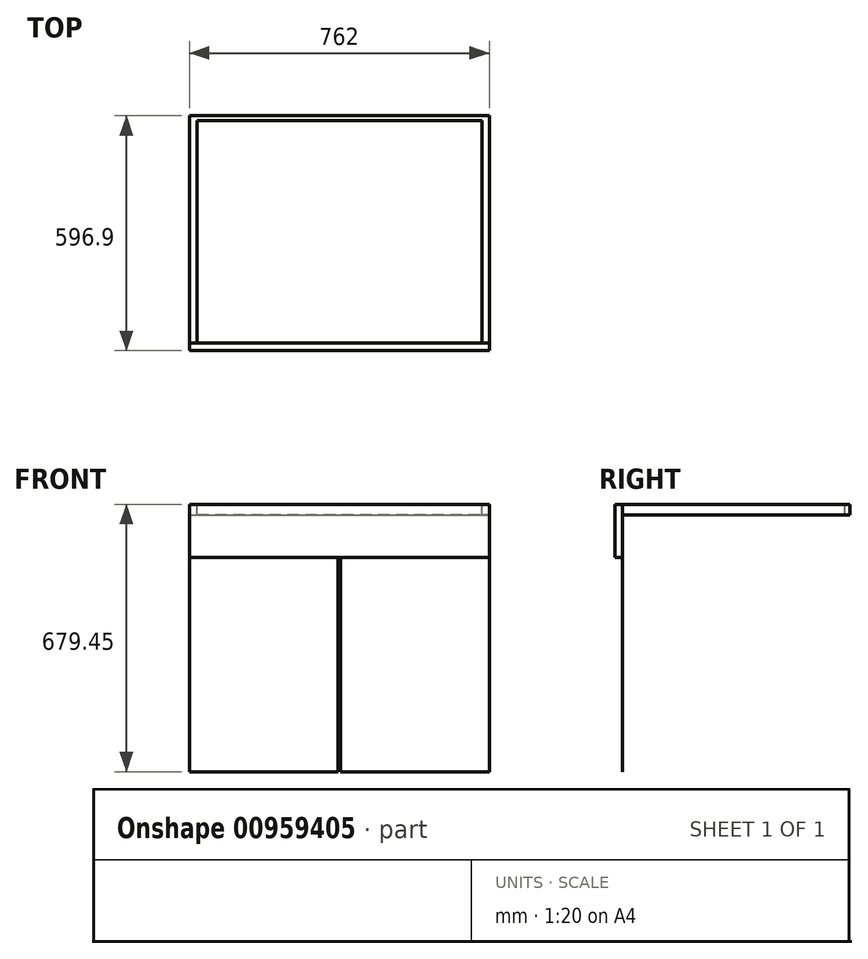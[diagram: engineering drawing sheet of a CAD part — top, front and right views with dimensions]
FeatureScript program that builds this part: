
annotation { "Feature Type Name" : "Feature", "Feature Type Description" : "" }
export const myFeature = defineFeature(function(context is Context, id is Id, definition is map)
    precondition{}
    {
        {
            assignVariable(context, id + "F0", {"name" : "depth", "anyValue" : 22.75});
        }
        {
            assignVariable(context, id + "F1", {"name" : "height", "anyValue" : 26.75});
        }
        {
            assignVariable(context, id + "F2", {"name" : "ply", "anyValue" : .75});
        }
        {
            assignVariable(context, id + "F3", {"name" : "back", "anyValue" : .5});
        }
        {
            var Q0;
            Q0=qCreatedBy(makeId("Top.planeOp"),FACE);
            var sketch = newSketch(context, id + "F4", { "sketchPlane" : qUnion([Q0])});
            skPoint(sketch, "E0.0", {"position": v(762, 508) * mm});
            skPoint(sketch, "E1.0", {"position": v(990.6, 0) * mm});
            skPoint(sketch, "E2.0", {"position": v(0, 577.85) * mm});
            skLineSegment(sketch, "E3.bottom", {"start": v(0, 577.85) * mm, "end": v(762, 577.85) * mm});
            skLineSegment(sketch, "E3.top", {"start": v(0, 565.15) * mm, "end": v(762, 565.15) * mm});
            skLineSegment(sketch, "E3.left", {"start": v(0, 577.85) * mm, "end": v(0, 565.15) * mm});
            skLineSegment(sketch, "E3.right", {"start": v(762, 577.85) * mm, "end": v(762, 565.15) * mm});
            skLineSegment(sketch, "E4.bottom", {"start": v(0, 565.15) * mm, "end": v(19.05, 565.15) * mm});
            skLineSegment(sketch, "E4.top", {"start": v(0, 0) * mm, "end": v(19.05, 0) * mm});
            skLineSegment(sketch, "E4.left", {"start": v(0, 565.15) * mm, "end": v(0, 0) * mm});
            skLineSegment(sketch, "E4.right", {"start": v(19.05, 565.15) * mm, "end": v(19.05, 0) * mm});
            skLineSegment(sketch, "E5.bottom", {"start": v(762, 565.15) * mm, "end": v(742.95, 565.15) * mm});
            skLineSegment(sketch, "E5.top", {"start": v(762, 0) * mm, "end": v(742.95, 0) * mm});
            skLineSegment(sketch, "E5.left", {"start": v(762, 565.15) * mm, "end": v(762, 0) * mm});
            skLineSegment(sketch, "E5.right", {"start": v(742.95, 565.15) * mm, "end": v(742.95, 0) * mm});
            skSolve(sketch);
        }
        {
            var Q0;
            Q0=qSketchRegion(id+"F4",true);
            extrude(context, id + "F5", {"entities" : qUnion([Q0]), "oppositeDirection" : true, "depth" : (getVariable(context, 'height')) * mm, "offsetDistance" : 25.4 * mm});
        }
        {
            var Q0;
            Q0=qCreatedBy(makeId("Top.planeOp"),FACE);
            var sketch = newSketch(context, id + "F6", { "sketchPlane" : qUnion([Q0])});
            skPoint(sketch, "E6.0", {"position": v(742.95, 0) * mm});
            skPoint(sketch, "E7.0", {"position": v(19.05, 565.15) * mm});
            skLineSegment(sketch, "E8.bottom", {"start": v(19.05, 565.15) * mm, "end": v(742.95, 565.15) * mm});
            skLineSegment(sketch, "E8.top", {"start": v(19.05, 0) * mm, "end": v(742.95, 0) * mm});
            skLineSegment(sketch, "E8.left", {"start": v(19.05, 565.15) * mm, "end": v(19.05, 0) * mm});
            skLineSegment(sketch, "E8.right", {"start": v(742.95, 565.15) * mm, "end": v(742.95, 0) * mm});
            skSolve(sketch);
        }
        {
            var Q0;
            Q0=qSketchRegion(id+"F6",true);
            extrude(context, id + "F7", {"entities" : qUnion([Q0]), "oppositeDirection" : true, "depth" : (getVariable(context, 'ply')) * mm, "offsetDistance" : 25.4 * mm});
        }
        {
            var Q0;
            Q0=makeQuery(id+"F5.opExtrude","CAP_FACE",FACE,{"disambiguationData":[OSD([sQuery(id+"F4.wireOp",EDGE,"E3.bottom"),sQuery(id+"F4.wireOp",EDGE,"E3.top"),sQuery(id+"F4.wireOp",EDGE,"E3.left"),sQuery(id+"F4.wireOp",EDGE,"E3.right"),sQuery(id+"F4.wireOp",EDGE,"E4.top"),sQuery(id+"F4.wireOp",EDGE,"E4.left"),sQuery(id+"F4.wireOp",EDGE,"E4.right"),sQuery(id+"F4.wireOp",EDGE,"E5.top"),sQuery(id+"F4.wireOp",EDGE,"E5.left"),sQuery(id+"F4.wireOp",EDGE,"E5.right")])],"isStart":false});
            var sketch = newSketch(context, id + "F8", { "sketchPlane" : qUnion([Q0])});
            skPoint(sketch, "E9.0", {"position": v(19.05, 0) * mm});
            skPoint(sketch, "E10.0", {"position": v(742.95, -565.15) * mm});
            skLineSegment(sketch, "E11.bottom", {"start": v(19.05, 0) * mm, "end": v(742.95, 0) * mm});
            skLineSegment(sketch, "E11.top", {"start": v(19.05, -565.15) * mm, "end": v(742.95, -565.15) * mm});
            skLineSegment(sketch, "E11.left", {"start": v(19.05, 0) * mm, "end": v(19.05, -565.15) * mm});
            skLineSegment(sketch, "E11.right", {"start": v(742.95, 0) * mm, "end": v(742.95, -565.15) * mm});
            skSolve(sketch);
        }
        {
            var Q0;
            Q0=qSketchRegion(id+"F8",true);
            extrude(context, id + "F9", {"entities" : qUnion([Q0]), "oppositeDirection" : true, "depth" : (getVariable(context, 'ply')) * mm, "offsetDistance" : 25.4 * mm});
        }
        {
            var Q0;
            Q0=makeQuery(id+"F5.opExtrude","SWEPT_FACE",FACE,{"disambiguationData":[OSD([sQuery(id+"F4.wireOp",EDGE,"E4.top")])]});
            var sketch = newSketch(context, id + "F10", { "sketchPlane" : qUnion([Q0])});
            skLineSegment(sketch, "E12.0", {"start": v(762, -679.45) * mm, "end": v(762, 0) * mm, "construction": true});
            skLineSegment(sketch, "E13.bottom", {"start": v(0, 0) * mm, "end": v(762, 0) * mm});
            skLineSegment(sketch, "E13.top", {"start": v(0, -135.73) * mm, "end": v(762, -135.73) * mm});
            skLineSegment(sketch, "E13.left", {"start": v(0, 0) * mm, "end": v(0, -135.73) * mm});
            skLineSegment(sketch, "E13.right", {"start": v(762, 0) * mm, "end": v(762, -135.73) * mm});
            skSolve(sketch);
        }
        {
            var Q0;
            Q0=qSketchRegion(id+"F10",true);
            extrude(context, id + "F11", {"entities" : qUnion([Q0]), "depth" : 19.05 * mm, "offsetDistance" : 25.4 * mm});
        }
        {
            var Q0;
            Q0=makeQuery(id+"F5.opExtrude","SWEPT_FACE",FACE,{"disambiguationData":[OSD([sQuery(id+"F4.wireOp",EDGE,"E3.top")])]});
            var sketch = newSketch(context, id + "F12", { "sketchPlane" : qUnion([Q0])});
            skLineSegment(sketch, "E14.0", {"start": v(19.05, -660.4) * mm, "end": v(742.95, -660.4) * mm, "construction": true});
            skLineSegment(sketch, "E15.0", {"start": v(19.05, -679.45) * mm, "end": v(19.05, 0) * mm, "construction": true});
            skLineSegment(sketch, "E16.0", {"start": v(742.95, -679.45) * mm, "end": v(742.95, 0) * mm, "construction": true});
            skLineSegment(sketch, "E17.bottom", {"start": v(19.05, -358.78) * mm, "end": v(742.95, -358.78) * mm});
            skLineSegment(sketch, "E17.top", {"start": v(19.05, -339.73) * mm, "end": v(742.95, -339.73) * mm});
            skLineSegment(sketch, "E17.left", {"start": v(19.05, -358.78) * mm, "end": v(19.05, -339.73) * mm});
            skLineSegment(sketch, "E17.right", {"start": v(742.95, -358.78) * mm, "end": v(742.95, -339.73) * mm});
            skLineSegment(sketch, "E18.0", {"start": v(0, 0) * mm, "end": v(762, 0) * mm, "construction": true});
            skSolve(sketch);
        }
        {
            var Q0;
            Q0=qSketchRegion(id+"F12",true);
            extrude(context, id + "F13", {"entities" : qUnion([Q0]), "depth" : (getVariable(context, 'depth') - getVariable(context, 'back')) * mm, "offsetDistance" : 25.4 * mm});
        }
        {
            var Q0;
            Q0=makeQuery(id+"F5.opExtrude","SWEPT_FACE",FACE,{"disambiguationData":[OSD([sQuery(id+"F4.wireOp",EDGE,"E5.top")])]});
            var sketch = newSketch(context, id + "F14", { "sketchPlane" : qUnion([Q0])});
            skLineSegment(sketch, "E19.0.1", {"start": v(742.95, -135.73) * mm, "end": v(742.95, -339.73) * mm});
            skLineSegment(sketch, "E19.0.2", {"start": v(742.95, -679.45) * mm, "end": v(762, -679.45) * mm});
            skLineSegment(sketch, "E19.0.3", {"start": v(762, -679.45) * mm, "end": v(762, -135.73) * mm});
            skLineSegment(sketch, "E20.0.0", {"start": v(742.95, -339.73) * mm, "end": v(19.05, -339.73) * mm});
            skLineSegment(sketch, "E20.0.2", {"start": v(19.05, -358.78) * mm, "end": v(742.95, -358.78) * mm});
            skLineSegment(sketch, "E20.0.3", {"start": v(742.95, -358.78) * mm, "end": v(742.95, -339.73) * mm});
            skLineSegment(sketch, "E21.0.1", {"start": v(0, -135.73) * mm, "end": v(0, -679.45) * mm});
            skLineSegment(sketch, "E21.0.2", {"start": v(0, -679.45) * mm, "end": v(19.05, -679.45) * mm});
            skLineSegment(sketch, "E21.0.3", {"start": v(19.05, -660.4) * mm, "end": v(19.05, -358.78) * mm});
            skLineSegment(sketch, "E22.0.0", {"start": v(19.05, -679.45) * mm, "end": v(742.95, -679.45) * mm});
            skLineSegment(sketch, "E22.0.1", {"start": v(742.95, -679.45) * mm, "end": v(742.95, -660.4) * mm});
            skLineSegment(sketch, "E22.0.2", {"start": v(742.95, -660.4) * mm, "end": v(19.05, -660.4) * mm});
            skLineSegment(sketch, "E23.trimOffspring", {"start": v(742.95, -358.78) * mm, "end": v(742.95, -660.4) * mm});
            skLineSegment(sketch, "E24.trimOffspring", {"start": v(19.05, -339.73) * mm, "end": v(19.05, -135.73) * mm});
            skLineSegment(sketch, "E25.0", {"start": v(0, -135.73) * mm, "end": v(19.05, -135.73) * mm});
            skLineSegment(sketch, "E26.trimOffspring", {"start": v(742.95, -135.73) * mm, "end": v(762, -135.73) * mm});
            skSolve(sketch);
        }
        {
            var Q0;
            Q0=qSketchRegion(id+"F14",true);
            extrude(context, id + "F15", {"entities" : qUnion([Q0]), "depth" : 19.05 * mm, "offsetDistance" : 25.4 * mm});
        }
        {
            var Q0;
            Q0=makeQuery(id+"F15.opExtrude","SWEPT_BODY",BODY,{"disambiguationData":[OSD([sQuery(id+"F14.wireOp",EDGE,"E19.0.1"),sQuery(id+"F14.wireOp",EDGE,"E19.0.2"),sQuery(id+"F14.wireOp",EDGE,"E19.0.3"),sQuery(id+"F14.wireOp",EDGE,"E20.0.0"),sQuery(id+"F14.wireOp",EDGE,"E20.0.2"),sQuery(id+"F14.wireOp",EDGE,"E21.0.1"),sQuery(id+"F14.wireOp",EDGE,"E21.0.2"),sQuery(id+"F14.wireOp",EDGE,"E21.0.3"),sQuery(id+"F14.wireOp",EDGE,"E22.0.0"),sQuery(id+"F14.wireOp",EDGE,"E22.0.2"),sQuery(id+"F14.wireOp",EDGE,"E23.trimOffspring"),sQuery(id+"F14.wireOp",EDGE,"E24.trimOffspring"),sQuery(id+"F14.wireOp",EDGE,"E25.0"),sQuery(id+"F14.wireOp",EDGE,"E26.trimOffspring")])]});
            deleteBodies(context, id + "F16", {"entities" : qUnion([Q0])});
        }
        {
            var Q0;
            Q0=makeQuery(id+"F13.opExtrude","SWEPT_BODY",BODY,{"disambiguationData":[OSD([sQuery(id+"F12.wireOp",EDGE,"E17.bottom"),sQuery(id+"F12.wireOp",EDGE,"E17.top"),sQuery(id+"F12.wireOp",EDGE,"E17.left"),sQuery(id+"F12.wireOp",EDGE,"E17.right")])]});
            deleteBodies(context, id + "F17", {"entities" : qUnion([Q0])});
        }
        {
            var Q0;
            Q0=qCreatedBy(makeId("Front.planeOp"),FACE);
            var sketch = newSketch(context, id + "F19", { "sketchPlane" : qUnion([Q0])});
            skPoint(sketch, "E27.0", {"position": v(0, -135.73) * mm});
            skPoint(sketch, "E28.0", {"position": v(762, -679.45) * mm});
            skPoint(sketch, "E29.0", {"position": v(0, -679.45) * mm});
            skLineSegment(sketch, "E30.bottom", {"start": v(0, -135.73) * mm, "end": v(377.83, -135.73) * mm});
            skLineSegment(sketch, "E30.top", {"start": v(0, -679.45) * mm, "end": v(377.83, -679.45) * mm});
            skLineSegment(sketch, "E30.left", {"start": v(0, -135.73) * mm, "end": v(0, -679.45) * mm});
            skLineSegment(sketch, "E30.right", {"start": v(377.83, -135.73) * mm, "end": v(377.83, -679.45) * mm});
            skLineSegment(sketch, "E31.bottom", {"start": v(762, -679.45) * mm, "end": v(384.18, -679.45) * mm});
            skLineSegment(sketch, "E31.top", {"start": v(762, -135.73) * mm, "end": v(384.18, -135.73) * mm});
            skLineSegment(sketch, "E31.left", {"start": v(762, -679.45) * mm, "end": v(762, -135.73) * mm});
            skLineSegment(sketch, "E31.right", {"start": v(384.18, -679.45) * mm, "end": v(384.18, -135.73) * mm});
            skSolve(sketch);
        }
        {
            var Q0;
            Q0=qSketchRegion(id+"F19",true);
            extrude(context, id + "F20", {"entities" : qUnion([Q0]), "depth" : (getVariable(context, 'ply')) * mm, "offsetDistance" : 25.4 * mm});
        }
    });
